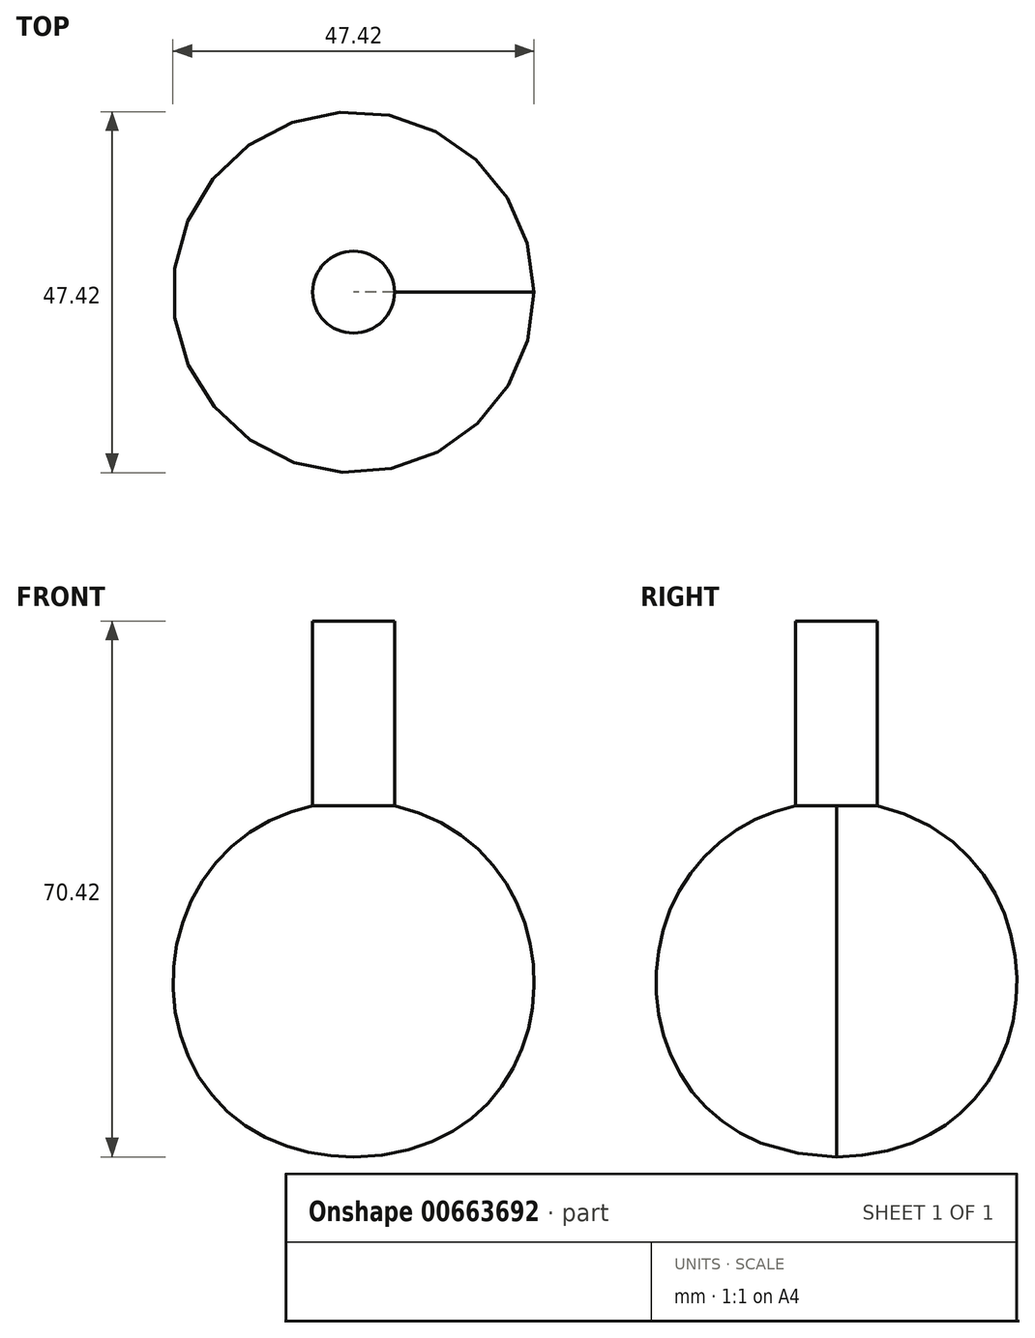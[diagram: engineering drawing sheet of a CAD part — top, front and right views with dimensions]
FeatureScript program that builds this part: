
annotation { "Feature Type Name" : "Feature", "Feature Type Description" : "" }
export const myFeature = defineFeature(function(context is Context, id is Id, definition is map)
    precondition{}
    {
        {
            var Q0;
            Q0=qCreatedBy(makeId("Front.planeOp"),FACE);
            var sketch = newSketch(context, id + "F0", { "sketchPlane" : qUnion([Q0])});
            skLineSegment(sketch, "E0", {"start": v(0, 22.95) * mm, "end": v(0, -23.87) * mm});
            skFitSpline(sketch, "E1", {"points": [v(0, 22.95) * mm, v(0, -23.87) * mm], "startDerivative": vector(93.74, -3.32) * mm, "endDerivative": vector(-95.96, -1.1) * mm});
            skLineSegment(sketch, "E2", {"start": v(0, 22.95) * mm, "end": v(0, 46.55) * mm});
            skLineSegment(sketch, "E3", {"start": v(5.38, 22.28) * mm, "end": v(5.38, 46.55) * mm});
            skLineSegment(sketch, "E4", {"start": v(0, 46.55) * mm, "end": v(5.38, 46.55) * mm});
            skSolve(sketch);
        }
        {
            var Q0;
            Q0=makeQuery(id+"F0.imprint","IMPRINT",FACE,{"disambiguationData":[TD([[makeQuery(id+"F0.imprint","IMPRINT",EDGE,{"derivedFrom":sQuery(id+"F0.wireOp",EDGE,"E0")}),1.0]])]});
            var Q1;
            Q1=sQuery(id+"F0.wireOp",EDGE,"E0");
            revolve(context, id + "F1", {"entities" : qUnion([Q0]), "axis" : qUnion([Q1]), "revolveType" : RevolveType.FULL});
        }
        {
            var Q0;
            {var subQ0=sQuery(id+"F0.wireOp",EDGE,"E2");Q0=makeQuery(id+"F0.imprint","IMPRINT",FACE,{"disambiguationData":[TD([[makeQuery(id+"F0.imprint","IMPRINT",EDGE,{"derivedFrom":subQ0}),-1.0]])]});}
            var Q1;
            Q1=sQuery(id+"F0.wireOp",EDGE,"E2");
            revolve(context, id + "F2", {"operationType" : NewBodyOperationType.ADD, "entities" : qUnion([Q0]), "axis" : qUnion([Q1]), "revolveType" : RevolveType.FULL});
        }
    });
